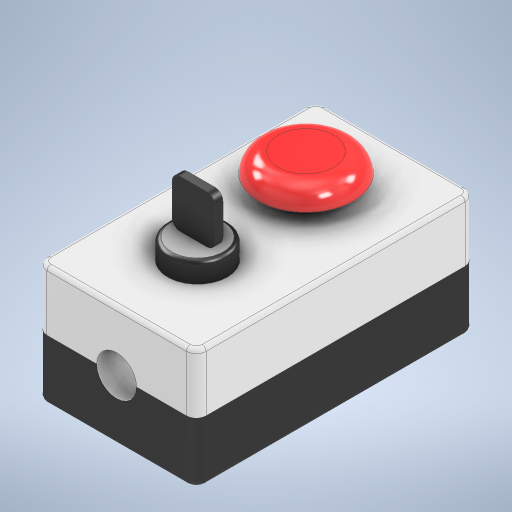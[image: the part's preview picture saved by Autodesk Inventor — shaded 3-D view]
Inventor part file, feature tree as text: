
AUTODESK INVENTOR PART (.ipt)
format: ipt  version: 2024 (Build 280153000, 153)  size: 409,088 bytes
history: native  units: in
note: dims shown in document units (in); Inventor stores cm internally (conversion verified against a paired STEP export)
features: extrude x8, sketch x8, fillet x5, projected_geometry x2
ambient origin geometry x8: Origin, YZ Plane, XZ Plane, XY Plane, X Axis, Y Axis, Z Axis, Center Point
bodies: Solid1 (feature_tree)
feature tree (23):
  extrude  "Extrusion1"  Depth=3.5in
  extrude  "Extrusion2"  Depth=0.75in TaperAngle=0.0deg
  fillet  "Fillet2"  Radius=0.001in
  extrude  "Extrusion3"  Depth=0.05in
  fillet  "Fillet3"  Radius=0.5in
  extrude  "Extrusion4"  Depth=0.25in TaperAngle=0.0deg
  fillet  "Fillet4"  Radius=0.05in
  fillet  "Fillet5"  Radius=1.2in
  extrude  "Extrusion5"  Depth=0.25in
  fillet  "Fillet6"  Radius=0.01in
  extrude  "Extrusion6"  Depth=0.05in
  sketch  "Sketch7"  dims[d22=0.54in d23=0.1in]
  extrude  "Extrusion7"  Depth=0.1in
  extrude  "Extrusion8"  Depth=0.1in
  sketch  "Sketch1"  dims[d0=2.0in d1=3.5in]
  sketch  "Sketch2"  dims[d2=0.125in d3=0.75in d4=0.0in d6=0.001in]
  projected_geometry  "Projected Loop1"
  sketch  "Sketch3"  dims[d7=0.75in d8=0.0in d9=0.05in d10=0.5in]
  sketch  "Sketch4"  dims[d11=0.75in d12=0.25in d13=0.0in d14=0.05in d15=1.2in]
  sketch  "Sketch5"  dims[d16=0.25in d17=0.0in d18=0.25in d19=0.01in]
  sketch  "Sketch6"  dims[d20=0.27in d21=0.05in]
  projected_geometry  "Projected Loop2"
  sketch  "Sketch8"  dims[d24=0.6in d25=0.0in d26=0.1in d27=0.1in d28=0.1in d29=0.1in d30=0.1in d31=0.6in d32=0.0in d33=0.5in d34=0.5in d35=1.0in d36=0.5in d37=0.0in d38=0.0in d39=1.0in d40=0.5in d41=0.0in d42=0.0in]
